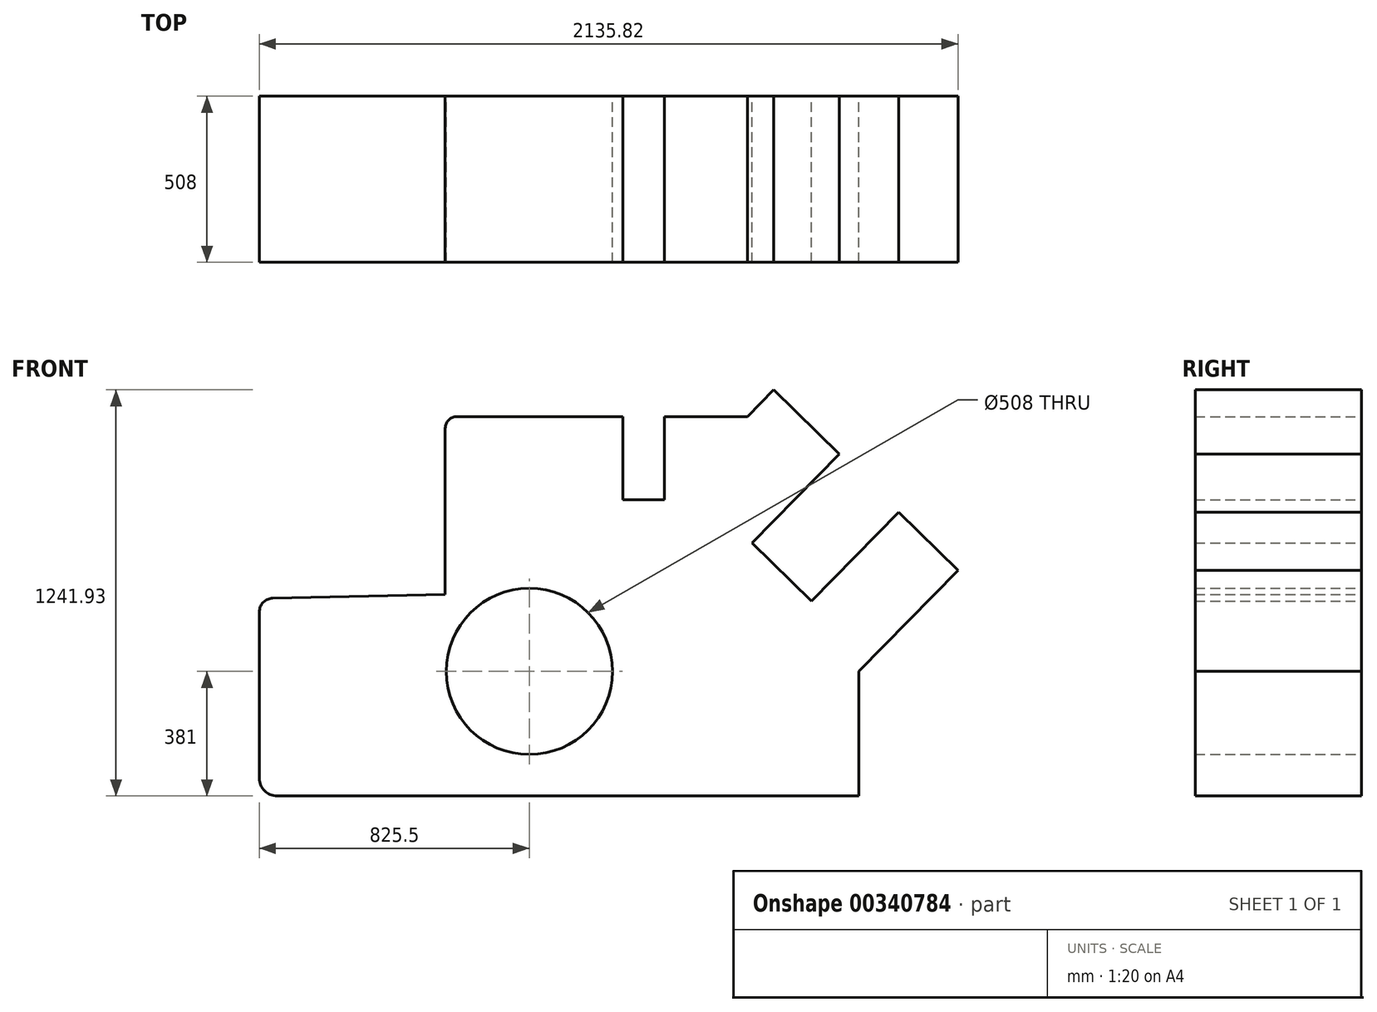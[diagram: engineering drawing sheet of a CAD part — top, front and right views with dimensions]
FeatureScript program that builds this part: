
annotation { "Feature Type Name" : "Feature", "Feature Type Description" : "" }
export const myFeature = defineFeature(function(context is Context, id is Id, definition is map)
    precondition{}
    {
        {
            var Q0;
            Q0=qCreatedBy(makeId("Front.planeOp"),FACE);
            var sketch = newSketch(context, id + "F0", { "sketchPlane" : qUnion([Q0])});
            skLineSegment(sketch, "E0", {"start": v(-549.2, 0) * mm, "end": v(1228.8, 0) * mm});
            skLineSegment(sketch, "E1", {"start": v(1228.8, 0) * mm, "end": v(1228.8, 381) * mm});
            skLineSegment(sketch, "E2", {"start": v(1228.8, 381) * mm, "end": v(1531.9, 690.58) * mm});
            skLineSegment(sketch, "E3", {"start": v(1531.9, 690.58) * mm, "end": v(1350.59, 868.1) * mm});
            skLineSegment(sketch, "E4", {"start": v(1350.59, 868.1) * mm, "end": v(1084.05, 595.85) * mm});
            skLineSegment(sketch, "E5", {"start": v(1084.05, 595.85) * mm, "end": v(902.55, 773.55) * mm});
            skLineSegment(sketch, "E6", {"start": v(902.55, 773.55) * mm, "end": v(1169.1, 1045.8) * mm});
            skLineSegment(sketch, "E7", {"start": v(1169.1, 1045.8) * mm, "end": v(968.76, 1241.93) * mm});
            skLineSegment(sketch, "E8", {"start": v(968.76, 1241.93) * mm, "end": v(889, 1160.46) * mm});
            skLineSegment(sketch, "E9", {"start": v(889, 1160.46) * mm, "end": v(635, 1160.46) * mm});
            skLineSegment(sketch, "E10", {"start": v(635, 1160.46) * mm, "end": v(635, 906.46) * mm});
            skLineSegment(sketch, "E11", {"start": v(635, 906.46) * mm, "end": v(508, 906.46) * mm});
            skLineSegment(sketch, "E12", {"start": v(508, 906.46) * mm, "end": v(508, 1160.46) * mm});
            skLineSegment(sketch, "E13", {"start": v(508, 1160.46) * mm, "end": v(0, 1160.46) * mm});
            skLineSegment(sketch, "E14", {"start": v(-603.92, 54.73) * mm, "end": v(-603.92, 562.73) * mm});
            skLineSegment(sketch, "E15", {"start": v(-35.51, 1124.95) * mm, "end": v(-35.51, 616.95) * mm});
            skLineSegment(sketch, "E16", {"start": v(-562.57, 605.02) * mm, "end": v(-35.51, 616.95) * mm});
            skArc(sketch, "E17", {"start": v(-603.92, 54.73) * mm, "mid": v(-587.9, 16.03) * mm, "end": v(-549.2, 0) * mm});
            skArc(sketch, "E18", {"start": v(-562.57, 605.02) * mm, "mid": v(-591.86, 592.3) * mm, "end": v(-603.92, 562.73) * mm});
            skArc(sketch, "E19", {"start": v(0, 1160.46) * mm, "mid": v(-25.11, 1150.06) * mm, "end": v(-35.51, 1124.95) * mm});
            skCircle(sketch, "E20", {"center": v(221.58, 381) * mm, "radius": 254 * mm});
            skSolve(sketch);
        }
        {
            var Q0;
            Q0 = qSketchRegion(id + "F0", true);
            extrude(context, id + "F1", {"entities" : qUnion([Q0]), "depth" : 508 * mm});
        }
    });
